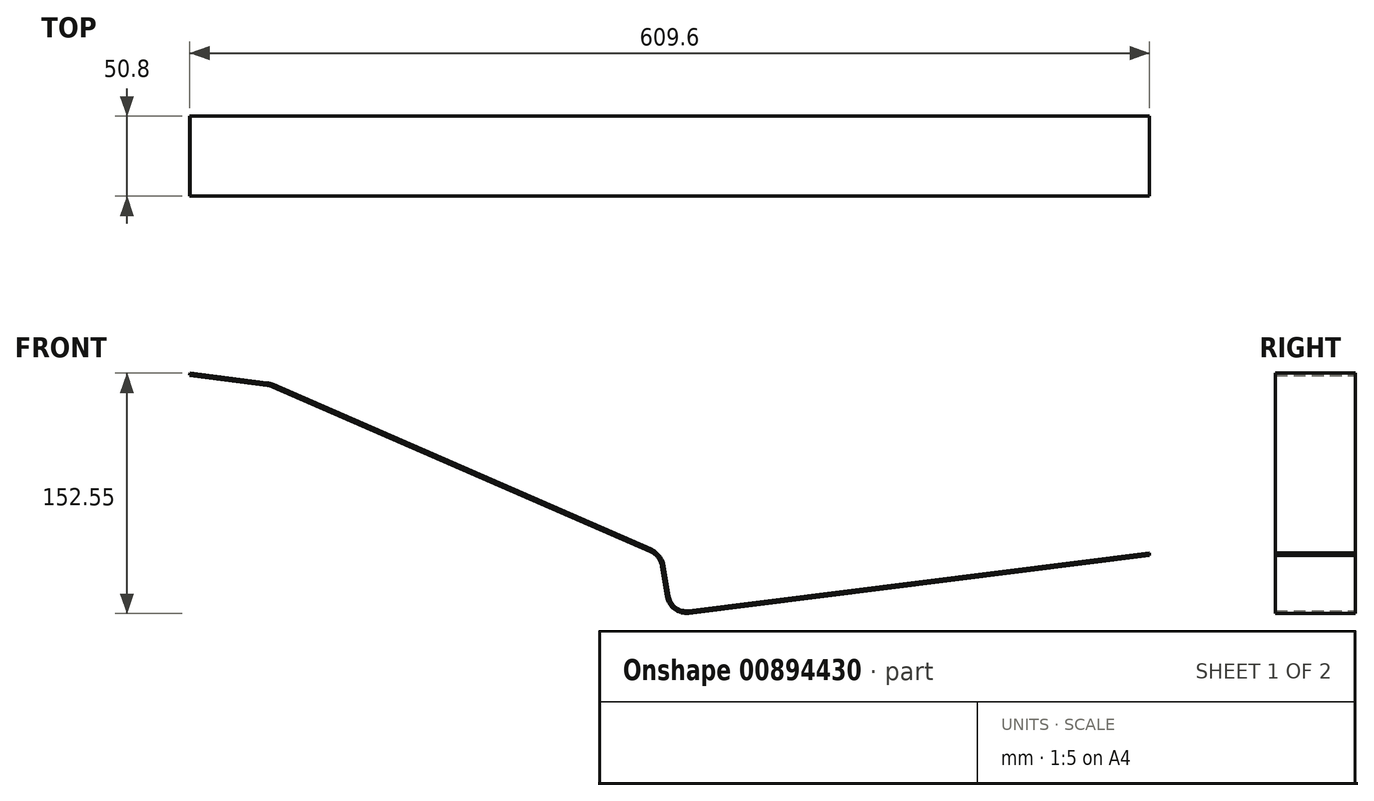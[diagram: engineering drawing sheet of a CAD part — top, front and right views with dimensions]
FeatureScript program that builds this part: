
annotation { "Feature Type Name" : "Feature", "Feature Type Description" : "" }
export const myFeature = defineFeature(function(context is Context, id is Id, definition is map)
    precondition{}
    {
        {
            var Q0;
            Q0=qCreatedBy(makeId("Front.planeOp"),FACE);
            var sketch = newSketch(context, id + "F0", { "sketchPlane" : qUnion([Q0])});
            skLineSegment(sketch, "E0", {"start": v(0, 0) * mm, "end": v(48.98, -6.12) * mm});
            skLineSegment(sketch, "E1", {"start": v(52.48, -7.08) * mm, "end": v(292.13, -111.55) * mm});
            skLineSegment(sketch, "E2", {"start": v(299.58, -121.1) * mm, "end": v(302.8, -140.37) * mm});
            skLineSegment(sketch, "E3", {"start": v(316.9, -150.89) * mm, "end": v(609.6, -114.3) * mm});
            skLineSegment(sketch, "E4", {"start": v(298.45, -114.3) * mm, "end": v(676.68, -114.3) * mm, "construction": true});
            skPoint(sketch, "E5.visualSharp", {"position": v(50.8, -6.35) * mm});
            skArc(sketch, "E5.filletArc", {"start": v(52.48, -7.08) * mm, "mid": v(50.77, -6.48) * mm, "end": v(48.98, -6.12) * mm});
            skPoint(sketch, "E6.visualSharp", {"position": v(298.45, -114.3) * mm});
            skArc(sketch, "E6.filletArc", {"start": v(299.58, -121.1) * mm, "mid": v(297.07, -115.38) * mm, "end": v(292.13, -111.55) * mm});
            skPoint(sketch, "E7.visualSharp", {"position": v(304.8, -152.4) * mm});
            skArc(sketch, "E7.filletArc", {"start": v(302.8, -140.37) * mm, "mid": v(307.73, -148.47) * mm, "end": v(316.9, -150.89) * mm});
            skLineSegment(sketch, "E8.0", {"start": v(316.7, -149.33) * mm, "end": v(609.4, -112.74) * mm});
            skArc(sketch, "E8.1", {"start": v(304.35, -140.11) * mm, "mid": v(308.67, -147.2) * mm, "end": v(316.7, -149.33) * mm});
            skLineSegment(sketch, "E8.2", {"start": v(301.14, -120.84) * mm, "end": v(304.35, -140.11) * mm});
            skLineSegment(sketch, "E8.3", {"start": v(0.2, 1.56) * mm, "end": v(49.18, -4.56) * mm});
            skArc(sketch, "E8.4", {"start": v(53.1, -5.64) * mm, "mid": v(51.18, -4.96) * mm, "end": v(49.18, -4.56) * mm});
            skLineSegment(sketch, "E8.5", {"start": v(53.1, -5.64) * mm, "end": v(292.76, -110.1) * mm});
            skArc(sketch, "E8.6", {"start": v(301.14, -120.84) * mm, "mid": v(298.31, -114.4) * mm, "end": v(292.76, -110.1) * mm});
            skLineSegment(sketch, "E9", {"start": v(0, 0) * mm, "end": v(0.2, 1.56) * mm});
            skLineSegment(sketch, "E10", {"start": v(609.4, -112.74) * mm, "end": v(609.6, -114.3) * mm});
            skSolve(sketch);
        }
        {
            var Q0;
            Q0 = qSketchRegion(id + "F0", true);
            extrude(context, id + "F1", {"entities" : qUnion([Q0]), "depth" : 25.4 * mm, "offsetDistance" : 25.4 * mm, "hasSecondDirection" : true, "secondDirectionOppositeDirection" : true, "secondDirectionDepth" : 25.4 * mm});
        }
    });
